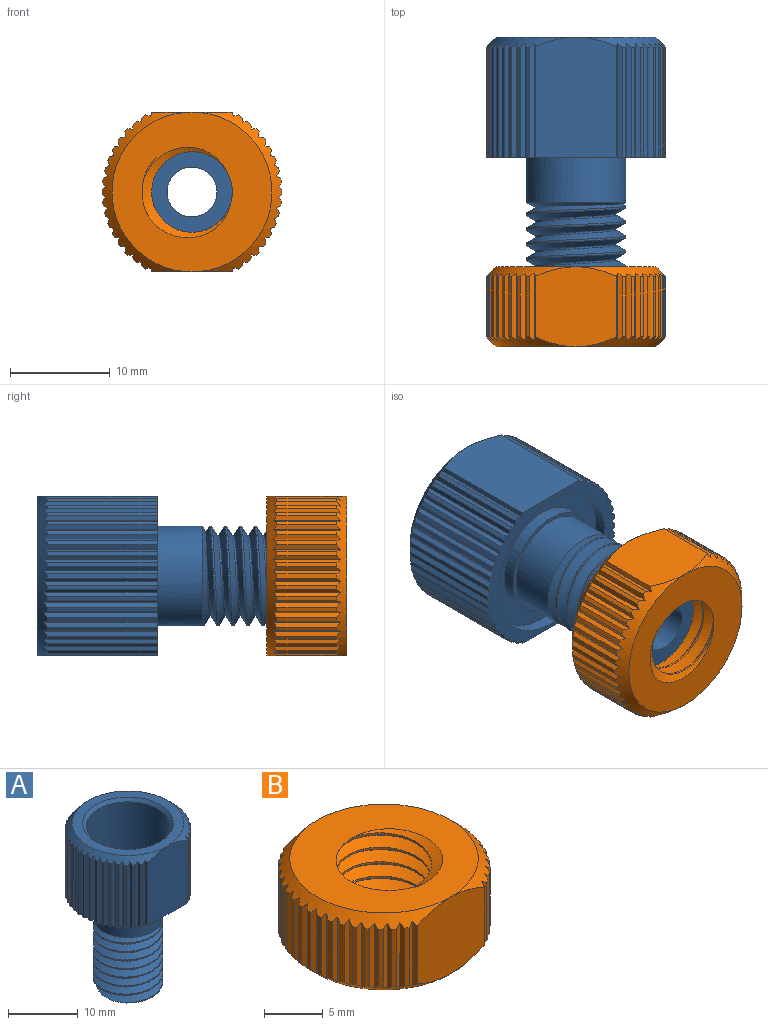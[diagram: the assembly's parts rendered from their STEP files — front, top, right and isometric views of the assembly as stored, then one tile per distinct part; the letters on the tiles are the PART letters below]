
ASSEMBLY  parts=2 mates=1
PART A: 138 faces, bbox 18.6x18.6x29.2 mm
  f0: cone r=6mm half-angle=45deg, axis (0,0,1), area 27.8mm2, adj f8,f59
  f1: cone r=3.3mm half-angle=45deg, axis (0,0,1), area 15.8mm2, adj f7,f60
  f2: cone r=2.5mm half-angle=45deg, axis (0,0,1), area 12.2mm2, adj f6,f61
  f3: cone r=8mm half-angle=45deg, axis (0,0,-1), area 26.7mm2, adj f20,f22,f23,f24,f25,f26,f27,f28
  f4: cylinder r=7.56mm len=15.12mm, axis (0,0,-1), area 59.4mm2, adj f58,f62
  f5: cylinder r=5.41mm len=10.82mm, axis (0,0,-1), area 42.5mm2, adj f55,f62
  f6: cylinder r=2.5mm len=12.5mm, axis (0,0,1), area 196.3mm2, adj f2,f137
  f7: cylinder r=3.3mm len=6.6mm, axis (0,0,1), area 114.1mm2, adj f1,f61
  f8: cylinder r=6mm len=12mm, axis (0,0,1), area 320.4mm2, adj f0,f60
  f9: cylinder r=5mm len=9.33mm, axis (0,0,1), area 2.1mm2, adj f10,f56,f57,f137
  f10: cylinder r=5mm len=10mm, axis (0,0,1), area 5.9mm2, adj f9,f11,f56,f57
  f11: cylinder r=5mm len=10mm, axis (0,0,1), area 5.9mm2, adj f10,f12,f56,f57
  f12: cylinder r=5mm len=10mm, axis (0,0,1), area 5.9mm2, adj f11,f13,f56,f57
  f13: cylinder r=5mm len=10mm, axis (0,0,1), area 5.9mm2, adj f12,f14,f56,f57
  f14: cylinder r=5mm len=10mm, axis (0,0,1), area 5.9mm2, adj f13,f15,f56,f57
  f15: cylinder r=5mm len=10mm, axis (0,0,1), area 5.9mm2, adj f14,f16,f56,f57
  f16: cylinder r=5mm len=10mm, axis (0,0,1), area 5.9mm2, adj f15,f17,f56,f57
  f17: cylinder r=5mm len=10mm, axis (0,0,1), area 144.5mm2, adj f16,f18,f55,f56,f57
  f18: cone r=4.03mm half-angle=65deg, axis (0,0,1), area 15.6mm2, adj f17,f19,f56,f57
  f19: cylinder r=4.03mm len=11mm, axis (0,0,-1), area 34.8mm2, adj f18,f56,f57,f137
  f20: cylinder r=9mm len=11mm, axis (0,0,-1), area 4.7mm2, adj f3,f58,f115,f118
  f21: cone r=8mm half-angle=45deg, axis (0,0,-1), area 26.7mm2, adj f38,f39,f40,f41,f42,f43,f44,f45
  f22: cylinder r=9mm len=11mm, axis (0,0,-1), area 4.7mm2, adj f3,f58,f131,f134
  f23: cylinder r=9mm len=11mm, axis (0,0,-1), area 4.7mm2, adj f3,f58,f129,f132
  f24: cylinder r=9mm len=11mm, axis (0,0,-1), area 4.7mm2, adj f3,f58,f127,f130
  f25: cylinder r=9mm len=11mm, axis (0,0,-1), area 4.7mm2, adj f3,f58,f125,f128
  f26: cylinder r=9mm len=11mm, axis (0,0,-1), area 4.7mm2, adj f3,f58,f123,f126
  f27: cylinder r=9mm len=11mm, axis (0,0,-1), area 4.7mm2, adj f3,f58,f121,f124
  f28: cylinder r=9mm len=11mm, axis (0,0,-1), area 4.7mm2, adj f3,f58,f119,f122
  f29: cylinder r=9mm len=11mm, axis (0,0,-1), area 4.7mm2, adj f3,f58,f117,f120
  f30: cylinder r=9mm len=11mm, axis (0,0,-1), area 4.7mm2, adj f3,f58,f113,f116
  f31: cylinder r=9mm len=11mm, axis (0,0,-1), area 4.7mm2, adj f3,f58,f111,f114
  f32: cylinder r=9mm len=11mm, axis (0,0,-1), area 4.7mm2, adj f3,f58,f109,f112
  f33: cylinder r=9mm len=11mm, axis (0,0,-1), area 4.7mm2, adj f3,f58,f107,f110
  f34: cylinder r=9mm len=11mm, axis (0,0,-1), area 4.7mm2, adj f3,f58,f105,f108
  f35: cylinder r=9mm len=11mm, axis (0,0,-1), area 4.7mm2, adj f3,f58,f103,f106
  f36: cylinder r=9mm len=11mm, axis (0,0,-1), area 4.7mm2, adj f3,f58,f101,f104
  f37: cylinder r=9mm len=11mm, axis (0,0,-1), area 4.7mm2, adj f3,f58,f99,f102
  f38: cylinder r=9mm len=11mm, axis (0,0,-1), area 4.7mm2, adj f21,f58,f95,f98
  f39: cylinder r=9mm len=11mm, axis (0,0,-1), area 4.7mm2, adj f21,f58,f93,f96
  f40: cylinder r=9mm len=11mm, axis (0,0,-1), area 4.7mm2, adj f21,f58,f91,f94
  f41: cylinder r=9mm len=11mm, axis (0,0,-1), area 4.7mm2, adj f21,f58,f89,f92
  f42: cylinder r=9mm len=11mm, axis (0,0,-1), area 4.7mm2, adj f21,f58,f87,f90
  f43: cylinder r=9mm len=11mm, axis (0,0,-1), area 4.7mm2, adj f21,f58,f85,f88
  f44: cylinder r=9mm len=11mm, axis (0,0,-1), area 4.7mm2, adj f21,f58,f83,f86
  f45: cylinder r=9mm len=11mm, axis (0,0,-1), area 4.7mm2, adj f21,f58,f81,f84
  f46: cylinder r=9mm len=11mm, axis (0,0,-1), area 4.7mm2, adj f21,f58,f79,f82
  f47: cylinder r=9mm len=11mm, axis (0,0,-1), area 4.7mm2, adj f21,f58,f77,f80
  f48: cylinder r=9mm len=11mm, axis (0,0,-1), area 4.7mm2, adj f21,f58,f75,f78
  f49: cylinder r=9mm len=11mm, axis (0,0,-1), area 4.7mm2, adj f21,f58,f73,f76
  f50: cylinder r=9mm len=11mm, axis (0,0,-1), area 4.7mm2, adj f21,f58,f71,f74
  f51: cylinder r=9mm len=11mm, axis (0,0,-1), area 4.7mm2, adj f21,f58,f69,f72
  f52: cylinder r=9mm len=11mm, axis (0,0,-1), area 4.7mm2, adj f21,f58,f67,f70
  f53: cylinder r=9mm len=11mm, axis (0,0,-1), area 4.7mm2, adj f21,f58,f65,f68
  f54: cylinder r=9mm len=11mm, axis (0,0,-1), area 4.7mm2, adj f21,f58,f63,f66
  f55: plane 10.82x10.82mm, normal (0,0,-1), area 13.4mm2, adj f5,f17
  f56: bspline ~12.13x10mm, area 239.2mm2, adj f9,f10,f11,f12,f13,f14,f15,f16
  f57: bspline ~12.58x10mm, area 239.2mm2, adj f9,f10,f11,f12,f13,f14,f15,f16
  f58: plane 18x16mm, normal (0,0,-1), area 59.2mm2, adj f4,f20,f22,f23,f24,f25,f26,f27
  f59: plane 16x16mm, normal (0,0,1), area 68.3mm2, adj f0,f3,f21
  f60: plane 12x12mm, normal (0,0,1), area 67.7mm2, adj f1,f8
  f61: plane 6.6x6.6mm, normal (0,0,1), area 6mm2, adj f2,f7
  f62: plane 15.12x15.12mm, normal (0,0,-1), area 87.6mm2, adj f4,f5
  f63: plane 11.37x0.49mm, normal (-0.28,0.96,0), area 5.6mm2, adj f21,f54,f58,f64
  f64: plane 11.37x0.44mm, normal (0.96,0.28,0), area 5mm2, adj f21,f58,f63,f135
  f65: plane 11.37x0.5mm, normal (-0.16,0.99,0), area 5.6mm2, adj f21,f53,f58,f66
  f66: plane 11.37x0.5mm, normal (0.99,0.16,0), area 5.6mm2, adj f21,f54,f58,f65
  f67: plane 11.37x0.51mm, normal (-0.03,1,0), area 5.6mm2, adj f21,f52,f58,f68
  f68: plane 11.37x0.51mm, normal (1,0.03,0), area 5.6mm2, adj f21,f53,f58,f67
  f69: plane 11.37x0.51mm, normal (0.09,1,0), area 5.6mm2, adj f21,f51,f58,f70
  f70: plane 11.37x0.51mm, normal (1,-0.09,0), area 5.6mm2, adj f21,f52,f58,f69
  f71: plane 11.37x0.5mm, normal (0.22,0.98,0), area 5.6mm2, adj f21,f50,f58,f72
  f72: plane 11.37x0.5mm, normal (0.98,-0.22,0), area 5.6mm2, adj f21,f51,f58,f71
  f73: plane 11.37x0.48mm, normal (0.34,0.94,0), area 5.6mm2, adj f21,f49,f58,f74
  f74: plane 11.37x0.48mm, normal (0.94,-0.34,0), area 5.6mm2, adj f21,f50,f58,f73
  f75: plane 11.37x0.45mm, normal (0.45,0.89,0), area 5.6mm2, adj f21,f48,f58,f76
  f76: plane 11.37x0.45mm, normal (0.89,-0.45,0), area 5.6mm2, adj f21,f49,f58,f75
  f77: plane 11.37x0.42mm, normal (0.56,0.83,0), area 5.6mm2, adj f21,f47,f58,f78
  f78: plane 11.37x0.42mm, normal (0.83,-0.56,0), area 5.6mm2, adj f21,f48,f58,f77
  f79: plane 11.37x0.38mm, normal (0.66,0.75,0), area 5.6mm2, adj f21,f46,f58,f80
  f80: plane 11.37x0.38mm, normal (0.75,-0.66,0), area 5.6mm2, adj f21,f47,f58,f79
  f81: plane 11.37x0.38mm, normal (0.75,0.66,0), area 5.6mm2, adj f21,f45,f58,f82
  f82: plane 11.37x0.38mm, normal (0.66,-0.75,0), area 5.6mm2, adj f21,f46,f58,f81
  f83: plane 11.37x0.42mm, normal (0.83,0.56,0), area 5.6mm2, adj f21,f44,f58,f84
  f84: plane 11.37x0.42mm, normal (0.56,-0.83,0), area 5.6mm2, adj f21,f45,f58,f83
  f85: plane 11.37x0.45mm, normal (0.89,0.45,0), area 5.6mm2, adj f21,f43,f58,f86
  f86: plane 11.37x0.45mm, normal (0.45,-0.89,0), area 5.6mm2, adj f21,f44,f58,f85
  f87: plane 11.37x0.48mm, normal (0.94,0.34,0), area 5.6mm2, adj f21,f42,f58,f88
  f88: plane 11.37x0.48mm, normal (0.34,-0.94,0), area 5.6mm2, adj f21,f43,f58,f87
  f89: plane 11.37x0.5mm, normal (0.98,0.22,0), area 5.6mm2, adj f21,f41,f58,f90
  f90: plane 11.37x0.5mm, normal (0.22,-0.98,0), area 5.6mm2, adj f21,f42,f58,f89
  f91: plane 11.37x0.51mm, normal (1,0.09,0), area 5.6mm2, adj f21,f40,f58,f92
  f92: plane 11.37x0.51mm, normal (0.09,-1,0), area 5.6mm2, adj f21,f41,f58,f91
  f93: plane 11.37x0.51mm, normal (1,-0.03,0), area 5.6mm2, adj f21,f39,f58,f94
  f94: plane 11.37x0.51mm, normal (-0.03,-1,0), area 5.6mm2, adj f21,f40,f58,f93
  f95: plane 11.37x0.5mm, normal (0.99,-0.16,0), area 5.6mm2, adj f21,f38,f58,f96
  f96: plane 11.37x0.5mm, normal (-0.16,-0.99,0), area 5.6mm2, adj f21,f39,f58,f95
  f97: plane 11.37x0.44mm, normal (0.96,-0.28,0), area 5mm2, adj f21,f58,f98,f136
  f98: plane 11.37x0.49mm, normal (-0.28,-0.96,0), area 5.6mm2, adj f21,f38,f58,f97
  f99: plane 11.37x0.49mm, normal (0.28,-0.96,0), area 5.6mm2, adj f3,f37,f58,f100
  f100: plane 11.37x0.44mm, normal (-0.96,-0.28,0), area 5mm2, adj f3,f58,f99,f136
  f101: plane 11.37x0.5mm, normal (0.16,-0.99,0), area 5.6mm2, adj f3,f36,f58,f102
  f102: plane 11.37x0.5mm, normal (-0.99,-0.16,0), area 5.6mm2, adj f3,f37,f58,f101
  f103: plane 11.37x0.51mm, normal (0.03,-1,0), area 5.6mm2, adj f3,f35,f58,f104
  f104: plane 11.37x0.51mm, normal (-1,-0.03,0), area 5.6mm2, adj f3,f36,f58,f103
  f105: plane 11.37x0.51mm, normal (-0.09,-1,0), area 5.6mm2, adj f3,f34,f58,f106
  f106: plane 11.37x0.51mm, normal (-1,0.09,0), area 5.6mm2, adj f3,f35,f58,f105
  f107: plane 11.37x0.5mm, normal (-0.22,-0.98,0), area 5.6mm2, adj f3,f33,f58,f108
  f108: plane 11.37x0.5mm, normal (-0.98,0.22,0), area 5.6mm2, adj f3,f34,f58,f107
  f109: plane 11.37x0.48mm, normal (-0.34,-0.94,0), area 5.6mm2, adj f3,f32,f58,f110
  f110: plane 11.37x0.48mm, normal (-0.94,0.34,0), area 5.6mm2, adj f3,f33,f58,f109
  f111: plane 11.37x0.45mm, normal (-0.45,-0.89,0), area 5.6mm2, adj f3,f31,f58,f112
  f112: plane 11.37x0.45mm, normal (-0.89,0.45,0), area 5.6mm2, adj f3,f32,f58,f111
  f113: plane 11.37x0.42mm, normal (-0.56,-0.83,0), area 5.6mm2, adj f3,f30,f58,f114
  f114: plane 11.37x0.42mm, normal (-0.83,0.56,0), area 5.6mm2, adj f3,f31,f58,f113
  f115: plane 11.37x0.38mm, normal (-0.66,-0.75,0), area 5.6mm2, adj f3,f20,f58,f116
  f116: plane 11.37x0.38mm, normal (-0.75,0.66,0), area 5.6mm2, adj f3,f30,f58,f115
  f117: plane 11.37x0.38mm, normal (-0.75,-0.66,0), area 5.6mm2, adj f3,f29,f58,f118
  f118: plane 11.37x0.38mm, normal (-0.66,0.75,0), area 5.6mm2, adj f3,f20,f58,f117
  f119: plane 11.37x0.42mm, normal (-0.83,-0.56,0), area 5.6mm2, adj f3,f28,f58,f120
  f120: plane 11.37x0.42mm, normal (-0.56,0.83,0), area 5.6mm2, adj f3,f29,f58,f119
  f121: plane 11.37x0.45mm, normal (-0.89,-0.45,0), area 5.6mm2, adj f3,f27,f58,f122
  f122: plane 11.37x0.45mm, normal (-0.45,0.89,0), area 5.6mm2, adj f3,f28,f58,f121
  f123: plane 11.37x0.48mm, normal (-0.94,-0.34,0), area 5.6mm2, adj f3,f26,f58,f124
  f124: plane 11.37x0.48mm, normal (-0.34,0.94,0), area 5.6mm2, adj f3,f27,f58,f123
  f125: plane 11.37x0.5mm, normal (-0.98,-0.22,0), area 5.6mm2, adj f3,f25,f58,f126
  f126: plane 11.37x0.5mm, normal (-0.22,0.98,0), area 5.6mm2, adj f3,f26,f58,f125
  f127: plane 11.37x0.51mm, normal (-1,-0.09,0), area 5.6mm2, adj f3,f24,f58,f128
  f128: plane 11.37x0.51mm, normal (-0.09,1,0), area 5.6mm2, adj f3,f25,f58,f127
  f129: plane 11.37x0.51mm, normal (-1,0.03,0), area 5.6mm2, adj f3,f23,f58,f130
  f130: plane 11.37x0.51mm, normal (0.03,1,0), area 5.6mm2, adj f3,f24,f58,f129
  f131: plane 11.37x0.5mm, normal (-0.99,0.16,0), area 5.6mm2, adj f3,f22,f58,f132
  f132: plane 11.37x0.5mm, normal (0.16,0.99,0), area 5.6mm2, adj f3,f23,f58,f131
  f133: plane 11.37x0.44mm, normal (-0.96,0.28,0), area 5mm2, adj f3,f58,f134,f135
  f134: plane 11.37x0.49mm, normal (0.28,0.96,0), area 5.6mm2, adj f3,f22,f58,f133
  f135: plane 12x8.08mm, normal (0,1,0), area 94.3mm2, adj f3,f21,f58,f64,f133
  f136: plane 12x8.08mm, normal (0,-1,0), area 94.2mm2, adj f3,f21,f58,f97,f100
  f137: plane 9.67x9.66mm, normal (0,0,-1), area 44.7mm2, adj f6,f9,f19,f56,f57
PART B: 118 faces, bbox 18.6x18.6x9.8 mm
  f0: cylinder r=4.03mm len=8.06mm, axis (0,0,1), area 25.9mm2, adj f39,f40,f114,f115
  f1: cone r=8mm half-angle=45deg, axis (0,0,-1), area 26.7mm2, adj f3,f6,f7,f8,f9,f10,f11,f12
  f2: cone r=9mm half-angle=45deg, axis (0,0,1), area 26.7mm2, adj f22,f23,f24,f25,f26,f27,f28,f29
  f3: cylinder r=9mm len=6mm, axis (0,0,-1), area 2.5mm2, adj f1,f4,f93,f96
  f4: cone r=9mm half-angle=45deg, axis (0,0,1), area 26.7mm2, adj f3,f6,f7,f8,f9,f10,f11,f12
  f5: cone r=8mm half-angle=45deg, axis (0,0,-1), area 26.7mm2, adj f22,f23,f24,f25,f26,f27,f28,f29
  f6: cylinder r=9mm len=6mm, axis (0,0,-1), area 2.5mm2, adj f1,f4,f109,f112
  f7: cylinder r=9mm len=6mm, axis (0,0,-1), area 2.5mm2, adj f1,f4,f107,f110
  f8: cylinder r=9mm len=6mm, axis (0,0,-1), area 2.5mm2, adj f1,f4,f105,f108
  f9: cylinder r=9mm len=6mm, axis (0,0,-1), area 2.5mm2, adj f1,f4,f103,f106
  f10: cylinder r=9mm len=6mm, axis (0,0,-1), area 2.5mm2, adj f1,f4,f101,f104
  f11: cylinder r=9mm len=6mm, axis (0,0,-1), area 2.5mm2, adj f1,f4,f99,f102
  f12: cylinder r=9mm len=6mm, axis (0,0,-1), area 2.5mm2, adj f1,f4,f97,f100
  f13: cylinder r=9mm len=6mm, axis (0,0,-1), area 2.5mm2, adj f1,f4,f95,f98
  f14: cylinder r=9mm len=6mm, axis (0,0,-1), area 2.5mm2, adj f1,f4,f91,f94
  f15: cylinder r=9mm len=6mm, axis (0,0,-1), area 2.5mm2, adj f1,f4,f89,f92
  f16: cylinder r=9mm len=6mm, axis (0,0,-1), area 2.5mm2, adj f1,f4,f87,f90
  f17: cylinder r=9mm len=6mm, axis (0,0,-1), area 2.5mm2, adj f1,f4,f85,f88
  f18: cylinder r=9mm len=6mm, axis (0,0,-1), area 2.5mm2, adj f1,f4,f83,f86
  f19: cylinder r=9mm len=6mm, axis (0,0,-1), area 2.5mm2, adj f1,f4,f81,f84
  f20: cylinder r=9mm len=6mm, axis (0,0,-1), area 2.5mm2, adj f1,f4,f79,f82
  f21: cylinder r=9mm len=6mm, axis (0,0,-1), area 2.5mm2, adj f1,f4,f77,f80
  f22: cylinder r=9mm len=6mm, axis (0,0,-1), area 2.5mm2, adj f2,f5,f73,f76
  f23: cylinder r=9mm len=6mm, axis (0,0,-1), area 2.5mm2, adj f2,f5,f71,f74
  f24: cylinder r=9mm len=6mm, axis (0,0,-1), area 2.5mm2, adj f2,f5,f69,f72
  f25: cylinder r=9mm len=6mm, axis (0,0,-1), area 2.5mm2, adj f2,f5,f67,f70
  f26: cylinder r=9mm len=6mm, axis (0,0,-1), area 2.5mm2, adj f2,f5,f65,f68
  f27: cylinder r=9mm len=6mm, axis (0,0,-1), area 2.5mm2, adj f2,f5,f63,f66
  f28: cylinder r=9mm len=6mm, axis (0,0,-1), area 2.5mm2, adj f2,f5,f61,f64
  f29: cylinder r=9mm len=6mm, axis (0,0,-1), area 2.5mm2, adj f2,f5,f59,f62
  f30: cylinder r=9mm len=6mm, axis (0,0,-1), area 2.5mm2, adj f2,f5,f57,f60
  f31: cylinder r=9mm len=6mm, axis (0,0,-1), area 2.5mm2, adj f2,f5,f55,f58
  f32: cylinder r=9mm len=6mm, axis (0,0,-1), area 2.5mm2, adj f2,f5,f53,f56
  f33: cylinder r=9mm len=6mm, axis (0,0,-1), area 2.5mm2, adj f2,f5,f51,f54
  f34: cylinder r=9mm len=6mm, axis (0,0,-1), area 2.5mm2, adj f2,f5,f49,f52
  f35: cylinder r=9mm len=6mm, axis (0,0,-1), area 2.5mm2, adj f2,f5,f47,f50
  f36: cylinder r=9mm len=6mm, axis (0,0,-1), area 2.5mm2, adj f2,f5,f45,f48
  f37: cylinder r=9mm len=6mm, axis (0,0,-1), area 2.5mm2, adj f2,f5,f43,f46
  f38: cylinder r=9mm len=6mm, axis (0,0,-1), area 2.5mm2, adj f2,f5,f41,f44
  f39: plane 16.6x16.6mm, normal (0,0,-1), area 136.7mm2, adj f0,f2,f4,f113,f114,f115
  f40: plane 16.58x16.58mm, normal (0,0,1), area 136.7mm2, adj f0,f1,f5,f113,f114,f115
  f41: plane 6.73x0.49mm, normal (-0.28,0.96,0), area 3.2mm2, adj f2,f5,f38,f42
  f42: plane 6.73x0.44mm, normal (0.96,0.28,0), area 2.9mm2, adj f2,f5,f41,f116
  f43: plane 6.73x0.5mm, normal (-0.16,0.99,0), area 3.2mm2, adj f2,f5,f37,f44
  f44: plane 6.73x0.5mm, normal (0.99,0.16,0), area 3.2mm2, adj f2,f5,f38,f43
  f45: plane 6.73x0.51mm, normal (-0.03,1,0), area 3.2mm2, adj f2,f5,f36,f46
  f46: plane 6.73x0.51mm, normal (1,0.03,0), area 3.2mm2, adj f2,f5,f37,f45
  f47: plane 6.73x0.51mm, normal (0.09,1,0), area 3.2mm2, adj f2,f5,f35,f48
  f48: plane 6.73x0.51mm, normal (1,-0.09,0), area 3.2mm2, adj f2,f5,f36,f47
  f49: plane 6.73x0.5mm, normal (0.22,0.98,0), area 3.2mm2, adj f2,f5,f34,f50
  f50: plane 6.73x0.5mm, normal (0.98,-0.22,0), area 3.2mm2, adj f2,f5,f35,f49
  f51: plane 6.73x0.48mm, normal (0.34,0.94,0), area 3.2mm2, adj f2,f5,f33,f52
  f52: plane 6.73x0.48mm, normal (0.94,-0.34,0), area 3.2mm2, adj f2,f5,f34,f51
  f53: plane 6.73x0.45mm, normal (0.45,0.89,0), area 3.2mm2, adj f2,f5,f32,f54
  f54: plane 6.73x0.45mm, normal (0.89,-0.45,0), area 3.2mm2, adj f2,f5,f33,f53
  f55: plane 6.73x0.42mm, normal (0.56,0.83,0), area 3.2mm2, adj f2,f5,f31,f56
  f56: plane 6.73x0.42mm, normal (0.83,-0.56,0), area 3.2mm2, adj f2,f5,f32,f55
  f57: plane 6.73x0.38mm, normal (0.66,0.75,0), area 3.2mm2, adj f2,f5,f30,f58
  f58: plane 6.73x0.38mm, normal (0.75,-0.66,0), area 3.2mm2, adj f2,f5,f31,f57
  f59: plane 6.73x0.38mm, normal (0.75,0.66,0), area 3.2mm2, adj f2,f5,f29,f60
  f60: plane 6.73x0.38mm, normal (0.66,-0.75,0), area 3.2mm2, adj f2,f5,f30,f59
  f61: plane 6.73x0.42mm, normal (0.83,0.56,0), area 3.2mm2, adj f2,f5,f28,f62
  f62: plane 6.73x0.42mm, normal (0.56,-0.83,0), area 3.2mm2, adj f2,f5,f29,f61
  f63: plane 6.73x0.45mm, normal (0.89,0.45,0), area 3.2mm2, adj f2,f5,f27,f64
  f64: plane 6.73x0.45mm, normal (0.45,-0.89,0), area 3.2mm2, adj f2,f5,f28,f63
  f65: plane 6.73x0.48mm, normal (0.94,0.34,0), area 3.2mm2, adj f2,f5,f26,f66
  f66: plane 6.73x0.48mm, normal (0.34,-0.94,0), area 3.2mm2, adj f2,f5,f27,f65
  f67: plane 6.73x0.5mm, normal (0.98,0.22,0), area 3.2mm2, adj f2,f5,f25,f68
  f68: plane 6.73x0.5mm, normal (0.22,-0.98,0), area 3.2mm2, adj f2,f5,f26,f67
  f69: plane 6.73x0.51mm, normal (1,0.09,0), area 3.2mm2, adj f2,f5,f24,f70
  f70: plane 6.73x0.51mm, normal (0.09,-1,0), area 3.2mm2, adj f2,f5,f25,f69
  f71: plane 6.73x0.51mm, normal (1,-0.03,0), area 3.2mm2, adj f2,f5,f23,f72
  f72: plane 6.73x0.51mm, normal (-0.03,-1,0), area 3.2mm2, adj f2,f5,f24,f71
  f73: plane 6.73x0.5mm, normal (0.99,-0.16,0), area 3.2mm2, adj f2,f5,f22,f74
  f74: plane 6.73x0.5mm, normal (-0.16,-0.99,0), area 3.2mm2, adj f2,f5,f23,f73
  f75: plane 6.73x0.44mm, normal (0.96,-0.28,0), area 2.9mm2, adj f2,f5,f76,f117
  f76: plane 6.73x0.49mm, normal (-0.28,-0.96,0), area 3.2mm2, adj f2,f5,f22,f75
  f77: plane 6.73x0.49mm, normal (0.28,-0.96,0), area 3.2mm2, adj f1,f4,f21,f78
  f78: plane 6.73x0.44mm, normal (-0.96,-0.28,0), area 2.9mm2, adj f1,f4,f77,f117
  f79: plane 6.73x0.5mm, normal (0.16,-0.99,0), area 3.2mm2, adj f1,f4,f20,f80
  f80: plane 6.73x0.5mm, normal (-0.99,-0.16,0), area 3.2mm2, adj f1,f4,f21,f79
  f81: plane 6.73x0.51mm, normal (0.03,-1,0), area 3.2mm2, adj f1,f4,f19,f82
  f82: plane 6.73x0.51mm, normal (-1,-0.03,0), area 3.2mm2, adj f1,f4,f20,f81
  f83: plane 6.73x0.51mm, normal (-0.09,-1,0), area 3.2mm2, adj f1,f4,f18,f84
  f84: plane 6.73x0.51mm, normal (-1,0.09,0), area 3.2mm2, adj f1,f4,f19,f83
  f85: plane 6.73x0.5mm, normal (-0.22,-0.98,0), area 3.2mm2, adj f1,f4,f17,f86
  f86: plane 6.73x0.5mm, normal (-0.98,0.22,0), area 3.2mm2, adj f1,f4,f18,f85
  f87: plane 6.73x0.48mm, normal (-0.34,-0.94,0), area 3.2mm2, adj f1,f4,f16,f88
  f88: plane 6.73x0.48mm, normal (-0.94,0.34,0), area 3.2mm2, adj f1,f4,f17,f87
  f89: plane 6.73x0.45mm, normal (-0.45,-0.89,0), area 3.2mm2, adj f1,f4,f15,f90
  f90: plane 6.73x0.45mm, normal (-0.89,0.45,0), area 3.2mm2, adj f1,f4,f16,f89
  f91: plane 6.73x0.42mm, normal (-0.56,-0.83,0), area 3.2mm2, adj f1,f4,f14,f92
  f92: plane 6.73x0.42mm, normal (-0.83,0.56,0), area 3.2mm2, adj f1,f4,f15,f91
  f93: plane 6.73x0.38mm, normal (-0.66,-0.75,0), area 3.2mm2, adj f1,f3,f4,f94
  f94: plane 6.73x0.38mm, normal (-0.75,0.66,0), area 3.2mm2, adj f1,f4,f14,f93
  f95: plane 6.73x0.38mm, normal (-0.75,-0.66,0), area 3.2mm2, adj f1,f4,f13,f96
  f96: plane 6.73x0.38mm, normal (-0.66,0.75,0), area 3.2mm2, adj f1,f3,f4,f95
  f97: plane 6.73x0.42mm, normal (-0.83,-0.56,0), area 3.2mm2, adj f1,f4,f12,f98
  f98: plane 6.73x0.42mm, normal (-0.56,0.83,0), area 3.2mm2, adj f1,f4,f13,f97
  f99: plane 6.73x0.45mm, normal (-0.89,-0.45,0), area 3.2mm2, adj f1,f4,f11,f100
  f100: plane 6.73x0.45mm, normal (-0.45,0.89,0), area 3.2mm2, adj f1,f4,f12,f99
  f101: plane 6.73x0.48mm, normal (-0.94,-0.34,0), area 3.2mm2, adj f1,f4,f10,f102
  f102: plane 6.73x0.48mm, normal (-0.34,0.94,0), area 3.2mm2, adj f1,f4,f11,f101
  f103: plane 6.73x0.5mm, normal (-0.98,-0.22,0), area 3.2mm2, adj f1,f4,f9,f104
  f104: plane 6.73x0.5mm, normal (-0.22,0.98,0), area 3.2mm2, adj f1,f4,f10,f103
  f105: plane 6.73x0.51mm, normal (-1,-0.09,0), area 3.2mm2, adj f1,f4,f8,f106
  f106: plane 6.73x0.51mm, normal (-0.09,1,0), area 3.2mm2, adj f1,f4,f9,f105
  f107: plane 6.73x0.51mm, normal (-1,0.03,0), area 3.2mm2, adj f1,f4,f7,f108
  f108: plane 6.73x0.51mm, normal (0.03,1,0), area 3.2mm2, adj f1,f4,f8,f107
  f109: plane 6.73x0.5mm, normal (-0.99,0.16,0), area 3.2mm2, adj f1,f4,f6,f110
  f110: plane 6.73x0.5mm, normal (0.16,0.99,0), area 3.2mm2, adj f1,f4,f7,f109
  f111: plane 6.73x0.44mm, normal (-0.96,0.28,0), area 2.9mm2, adj f1,f4,f112,f116
  f112: plane 6.73x0.49mm, normal (0.28,0.96,0), area 3.2mm2, adj f1,f4,f6,f111
  f113: cylinder r=5mm len=10mm, axis (0,0,-1), area 31.3mm2, adj f39,f40,f114,f115
  f114: bspline ~10x10mm, area 169.4mm2, adj f0,f39,f40,f113
  f115: bspline ~10x10mm, area 169.6mm2, adj f0,f39,f40,f113
  f116: plane 8.08x8mm, normal (0,1,0), area 59.3mm2, adj f1,f2,f4,f5,f42,f111
  f117: plane 8.08x8mm, normal (0,-1,0), area 59.3mm2, adj f1,f2,f4,f5,f75,f78
PLACE A rot(axis=(-1,0,0),90deg) t=(-99.34,65.64,11.22)mm
PLACE B rot(axis=(-1,0,0),90deg) t=(-99.34,46.67,11.22)mm
MATE slider A.f4 <-> B.f0  axis (0,-1,0) through (-99.34,66.27,11.22)mm
